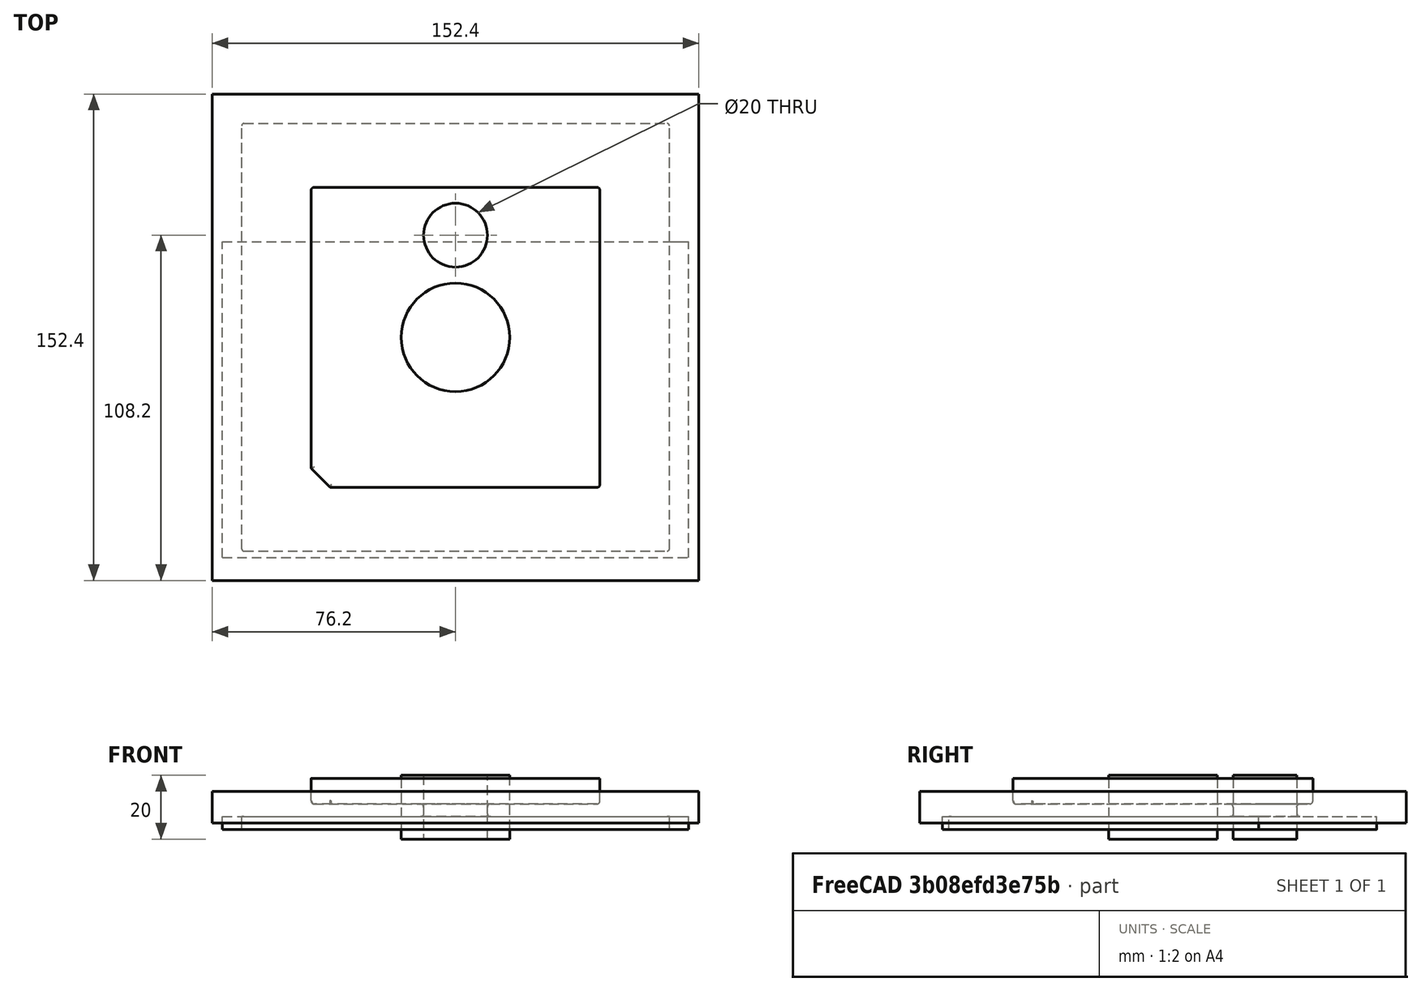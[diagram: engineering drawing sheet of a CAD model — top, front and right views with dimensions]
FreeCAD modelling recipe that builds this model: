
FCSTD DOCUMENT  (FreeCAD 0.21R33771 (Git))
Label: floppy_scan_frame_2
License: All rights reserved
LicenseURL: http://en.wikipedia.org/wiki/All_rights_reserved
objects: PartDesign::Fillet×8, PartDesign::Body×6, App::Part×5, PartDesign::AdditiveBox×4, PartDesign::Chamfer×2, PartDesign::Boolean×2, PartDesign::AdditiveCylinder×2
note: 40 computed .brp shape members not serialized (recipe doc carries the construction recipe); baked Part::Feature solids carry a one-line shape summary decoded from their .brp

FEATURE [App::Part] Part001  label="3.5 floppy cutout"
  Origin = -> Origin003
FEATURE [PartDesign::AdditiveBox] Box
  AttacherType = Attacher::AttachEngine3D
  AttachmentOffset = pos=(-76.2,-76.2,0) rot=(0,0,1;0rad)
  Height = 10
  Length = 152.4
  MapMode = 5
  Placement = pos=(-76.2,-76.2,0) rot=(0,0,1;0rad)
  Support = -> [XY_Plane002]
  Width = 152.4
FEATURE [PartDesign::AdditiveBox] Box001
  AttacherType = Attacher::AttachEngine3D
  AttachmentOffset = pos=(-45.25,-47,6) rot=(0,0,1;0rad)
  Height = 8
  Length = 90.5
  MapMode = 5
  Placement = pos=(-45.25,-47,6) rot=(0,0,1;0rad)
  Support = -> [XY_Plane004]
  Width = 94
FEATURE [PartDesign::Chamfer] Chamfer
  Angle = 45
  Base = -> Box001 [Edge1]
  BaseFeature = -> Box001
  ChamferType = 0
  FlipDirection = false
  Placement = pos=(-45.25,-47,6) rot=(0,0,1;0rad)
  Size = 6
  Size2 = 1
  SupportTransform = false
  UseAllEdges = false
FEATURE [PartDesign::Fillet] Fillet
  Base = -> Chamfer [Edge12,Edge3,Edge15]
  BaseFeature = -> Chamfer
  Placement = pos=(-45.25,-47,6) rot=(0,0,1;0rad)
  Radius = 1
  SupportTransform = false
  UseAllEdges = false
FEATURE [PartDesign::Fillet] Fillet001
  Base = -> Fillet [Edge3,Edge15]
  BaseFeature = -> Fillet
  Placement = pos=(-45.25,-47,6) rot=(0,0,1;0rad)
  Radius = 0.5
  SupportTransform = false
  UseAllEdges = false
FEATURE [PartDesign::Fillet] Fillet002
  Base = -> Fillet001 [Edge4,Edge14,Edge18,Edge22,Edge20,Edge24,Edge23,Edge21,Edge19,Edge16]
  BaseFeature = -> Fillet001
  Placement = pos=(-45.25,-47,6) rot=(0,0,1;0rad)
  Radius = 1
  SupportTransform = false
  UseAllEdges = false
FEATURE [PartDesign::Body] Body
  Group = -> [Box001,Chamfer,Fillet,Fillet001,Fillet002]
  Origin = -> Origin004
  Tip = -> Fillet002
FEATURE [App::Part] Part002  label="5.25 floppy cutout"
  Origin = -> Origin005
FEATURE [PartDesign::AdditiveBox] Box002
  AttacherType = Attacher::AttachEngine3D
  AttachmentOffset = pos=(-67,-67,-2) rot=(0,0,1;0rad)
  Height = 4
  Length = 134
  MapMode = 5
  Placement = pos=(-67,-67,-2) rot=(0,0,1;0rad)
  Support = -> [XY_Plane006]
  Width = 134
FEATURE [PartDesign::Chamfer] Chamfer001
  Angle = 45
  Base = -> Box002 [Edge1,Edge3,Edge7,Edge5]
  BaseFeature = -> Box002
  ChamferType = 0
  FlipDirection = false
  Placement = pos=(-67,-67,-2) rot=(0,0,1;0rad)
  Size = 0.5
  Size2 = 1
  SupportTransform = false
  UseAllEdges = false
FEATURE [PartDesign::Fillet] Fillet003
  Base = -> Chamfer001 [Edge13,Edge2]
  BaseFeature = -> Chamfer001
  Placement = pos=(-67,-67,-2) rot=(0,0,1;0rad)
  Radius = 0.5
  SupportTransform = false
  UseAllEdges = false
FEATURE [PartDesign::Fillet] Fillet004
  Base = -> Fillet003 [Edge30,Edge29]
  BaseFeature = -> Fillet003
  Placement = pos=(-67,-67,-2) rot=(0,0,1;0rad)
  Radius = 0.5
  SupportTransform = false
  UseAllEdges = false
FEATURE [PartDesign::Fillet] Fillet005
  Base = -> Fillet004 [Edge28,Edge33]
  BaseFeature = -> Fillet004
  Placement = pos=(-67,-67,-2) rot=(0,0,1;0rad)
  Radius = 0.5
  SupportTransform = false
  UseAllEdges = false
FEATURE [PartDesign::Fillet] Fillet006
  Base = -> Fillet005 [Edge35,Edge31]
  BaseFeature = -> Fillet005
  Placement = pos=(-67,-67,-2) rot=(0,0,1;0rad)
  Radius = 0.5
  SupportTransform = false
  UseAllEdges = false
FEATURE [PartDesign::Body] Body002
  Group = -> [Box002,Chamfer001,Fillet003,Fillet004,Fillet005,Fillet006]
  Origin = -> Origin006
  Tip = -> Fillet006
FEATURE [App::Part] Part003  label="5.25 sleeve cutout"
  Origin = -> Origin007
FEATURE [PartDesign::AdditiveBox] Box003
  AttacherType = Attacher::AttachEngine3D
  AttachmentOffset = pos=(-73,-69,-2) rot=(0,0,1;0rad)
  Height = 4
  Length = 146
  MapMode = 5
  Placement = pos=(-73,-69,-2) rot=(0,0,1;0rad)
  Support = -> [XY_Plane008]
  Width = 99
FEATURE [PartDesign::Body] Body003
  Group = -> [Box003]
  Origin = -> Origin008
  Tip = -> Box003
FEATURE [PartDesign::Boolean] Boolean
  BaseFeature = -> Box
  Group = -> [Body]
  Type = 1
FEATURE [PartDesign::AdditiveCylinder] Cylinder
  Angle = 360
  AttacherType = Attacher::AttachEngine3D
  AttachmentOffset = pos=(0,32,-5) rot=(0,0,1;0rad)
  FirstAngle = 0
  Height = 20
  MapMode = 5
  Placement = pos=(0,32,-5) rot=(0,0,1;0rad)
  Radius = 10
  SecondAngle = 0
  Support = -> [XY_Plane010]
FEATURE [PartDesign::Body] Body004
  Group = -> [Cylinder]
  Origin = -> Origin010
  Tip = -> Cylinder
FEATURE [PartDesign::Boolean] Boolean001
  BaseFeature = -> Boolean
  Group = -> [Body002,Body003,Body004]
  Type = 1
FEATURE [PartDesign::AdditiveCylinder] Cylinder001
  Angle = 360
  AttacherType = Attacher::AttachEngine3D
  AttachmentOffset = pos=(0,0,-5) rot=(0,0,1;0rad)
  FirstAngle = 0
  Height = 20
  MapMode = 5
  Placement = pos=(0,0,-5) rot=(0,0,1;0rad)
  Radius = 17
  SecondAngle = 0
  Support = -> [XY_Plane011]
FEATURE [PartDesign::Body] Body005
  Group = -> [Cylinder001]
  Origin = -> Origin011
  Tip = -> Cylinder001
FEATURE [App::Part] Part004  label="finger hole"
  Group = -> [Body005]
  Origin = -> Origin009
FEATURE [PartDesign::Fillet] Fillet007
  Base = -> Boolean001 [Face45]
  BaseFeature = -> Boolean001
  Radius = 1
  SupportTransform = false
  UseAllEdges = false
FEATURE [PartDesign::Body] Body001  label="base"
  Group = -> [Box,Boolean,Boolean001,Fillet007]
  Origin = -> Origin002
  Tip = -> Fillet007
FEATURE [App::Part] Part  label="base001"
  Group = -> [Body001]
  Origin = -> Origin
